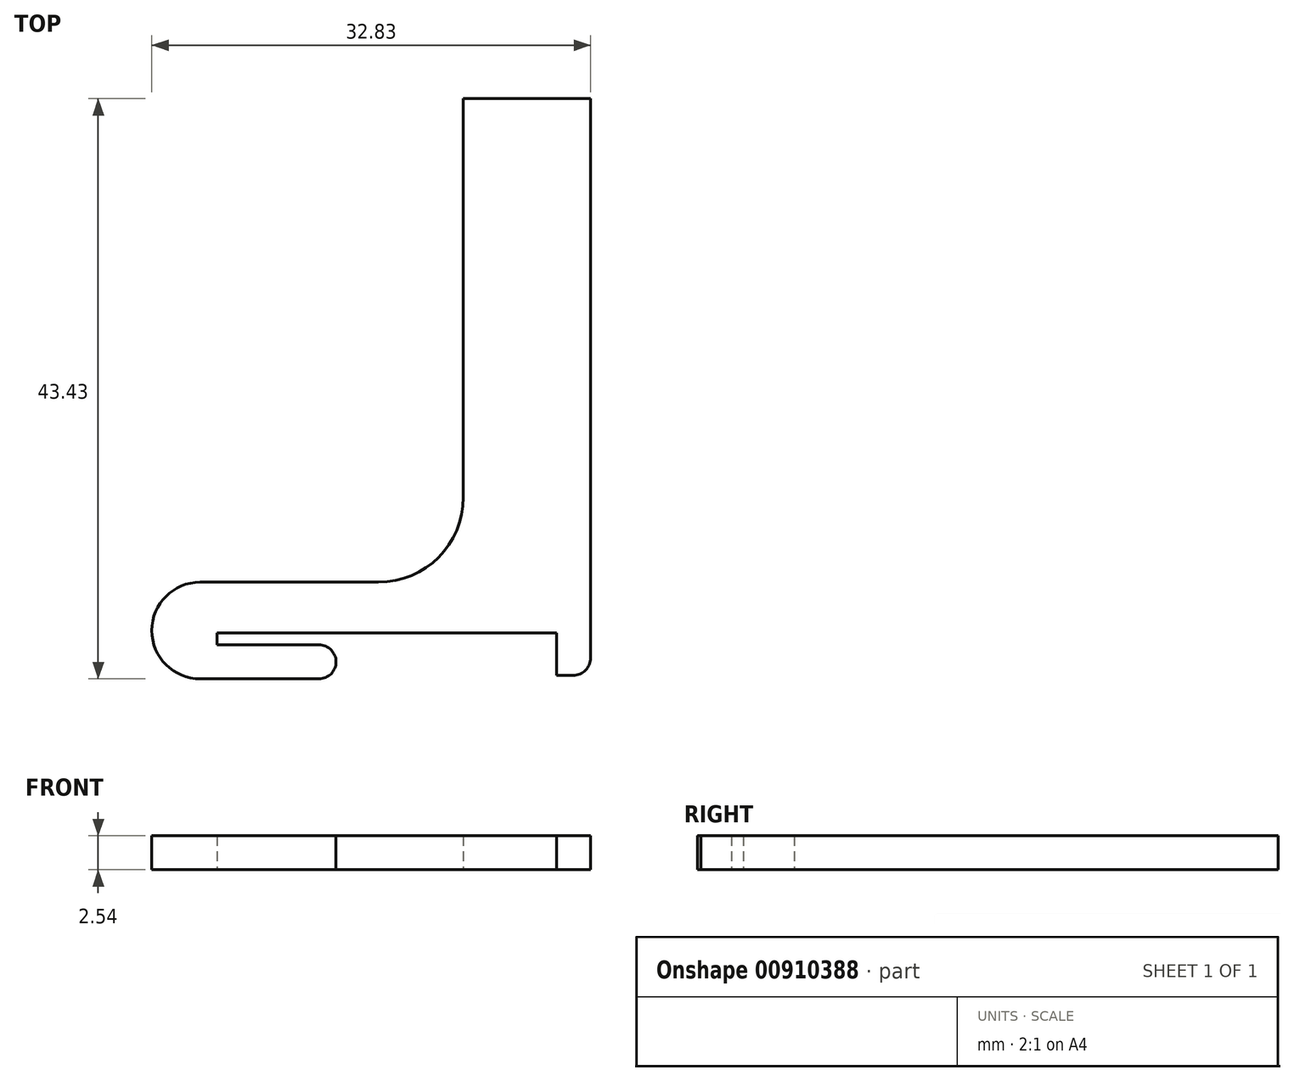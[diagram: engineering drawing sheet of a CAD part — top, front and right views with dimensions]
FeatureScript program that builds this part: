
annotation { "Feature Type Name" : "Feature", "Feature Type Description" : "" }
export const myFeature = defineFeature(function(context is Context, id is Id, definition is map)
    precondition{}
    {
        {
            var Q0;
            Q0=qCreatedBy(makeId("Top.planeOp"),FACE);
            var sketch = newSketch(context, id + "F0", { "sketchPlane" : qUnion([Q0])});
            skLineSegment(sketch, "E0", {"start": v(-6.99, 40) * mm, "end": v(-6.99, 10.16) * mm});
            skLineSegment(sketch, "E1", {"start": v(-13.34, 3.8) * mm, "end": v(-26.67, 3.8) * mm});
            skLineSegment(sketch, "E2", {"start": v(-26.67, -3.43) * mm, "end": v(-17.78, -3.43) * mm});
            skLineSegment(sketch, "E3", {"start": v(-17.78, -0.89) * mm, "end": v(-25.4, -0.89) * mm});
            skLineSegment(sketch, "E4", {"start": v(-25.4, -0.89) * mm, "end": v(-25.4, 0) * mm});
            skLineSegment(sketch, "E5", {"start": v(-25.4, 0) * mm, "end": v(0, 0) * mm});
            skLineSegment(sketch, "E6", {"start": v(0, 0) * mm, "end": v(0, -3.18) * mm});
            skLineSegment(sketch, "E7", {"start": v(0, -3.18) * mm, "end": v(1.22, -3.18) * mm});
            skLineSegment(sketch, "E8", {"start": v(2.54, -1.85) * mm, "end": v(2.54, 40) * mm});
            skLineSegment(sketch, "E9", {"start": v(2.54, 40) * mm, "end": v(-6.99, 40) * mm});
            skArc(sketch, "E10", {"start": v(-26.67, 3.8) * mm, "mid": v(-30.29, 0.2) * mm, "end": v(-26.67, -3.43) * mm});
            skPoint(sketch, "E11.visualSharp", {"position": v(-6.99, 3.81) * mm});
            skArc(sketch, "E11.filletArc", {"start": v(-13.34, 3.8) * mm, "mid": v(-8.84, 5.67) * mm, "end": v(-6.99, 10.16) * mm});
            skPoint(sketch, "E12.visualSharp", {"position": v(2.54, -3.18) * mm});
            skArc(sketch, "E12.filletArc", {"start": v(1.22, -3.18) * mm, "mid": v(2.15, -2.79) * mm, "end": v(2.54, -1.85) * mm});
            skArc(sketch, "E13", {"start": v(-17.78, -3.43) * mm, "mid": v(-16.51, -2.16) * mm, "end": v(-17.78, -0.89) * mm});
            skSolve(sketch);
        }
        {
            var Q0;
            Q0=qSketchRegion(id+"F0",true);
            extrude(context, id + "F1", {"entities" : qUnion([Q0]), "depth" : 2.54 * mm, "offsetDistance" : 25.4 * mm});
        }
    });
